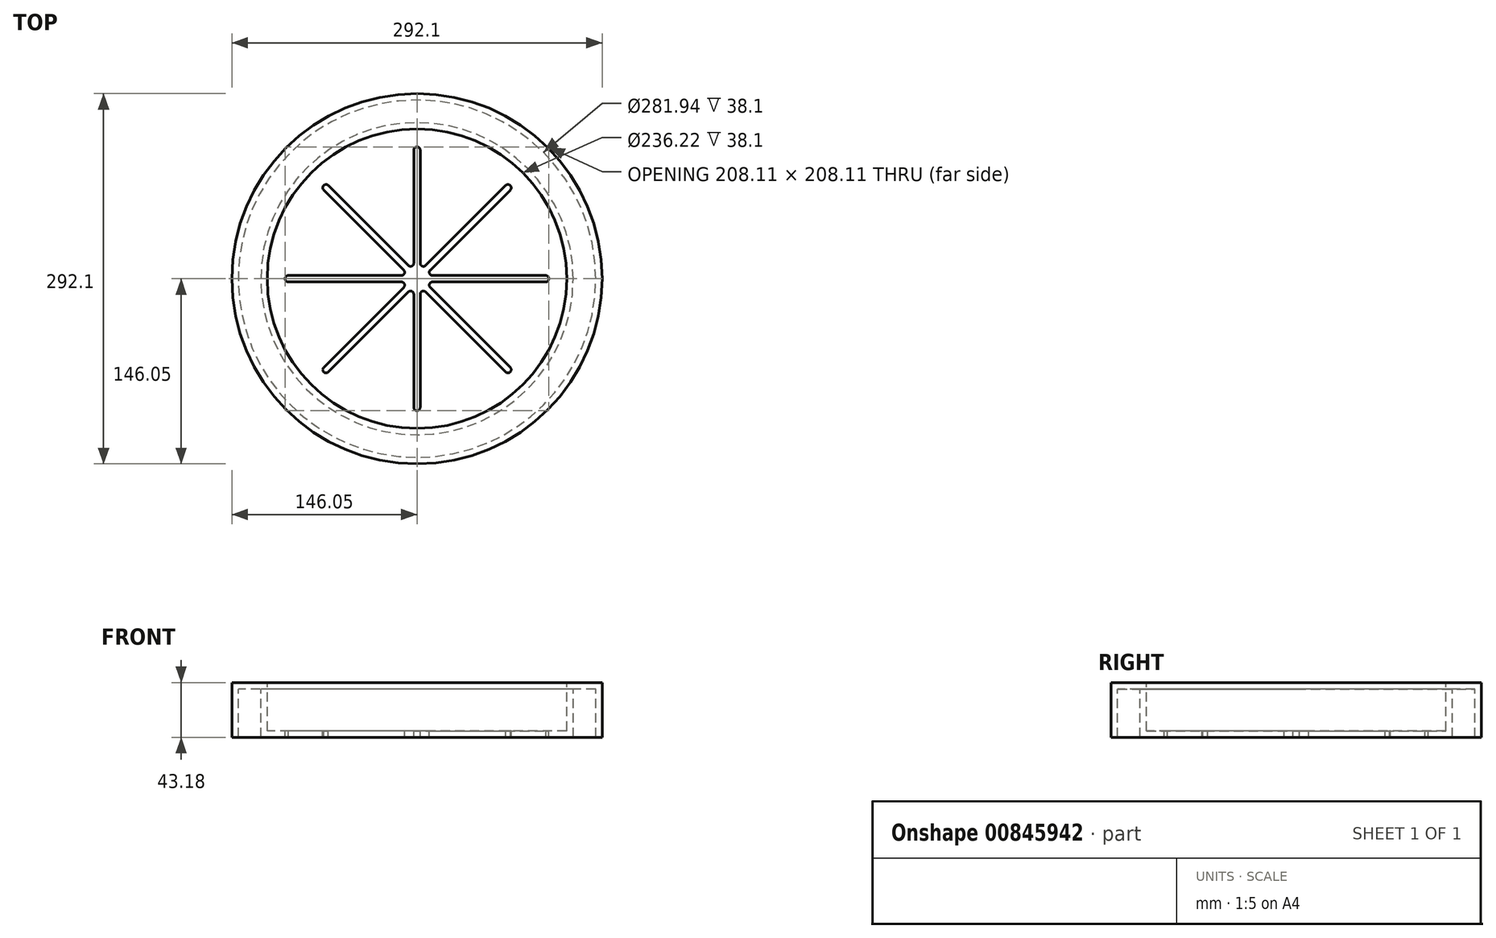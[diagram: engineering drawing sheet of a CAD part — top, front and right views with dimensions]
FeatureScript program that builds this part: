
annotation { "Feature Type Name" : "Feature", "Feature Type Description" : "" }
export const myFeature = defineFeature(function(context is Context, id is Id, definition is map)
    precondition{}
    {
        {
            var Q0;
            Q0=qCreatedBy(makeId("Front.planeOp"),FACE);
            var sketch = newSketch(context, id + "F0", { "sketchPlane" : qUnion([Q0])});
            skLineSegment(sketch, "E0", {"start": v(0, 0) * mm, "end": v(-123.2, 0) * mm});
            skLineSegment(sketch, "E1", {"start": v(-146.05, 0) * mm, "end": v(-146.05, 43.18) * mm});
            skLineSegment(sketch, "E2", {"start": v(-146.05, 43.18) * mm, "end": v(-118.11, 43.18) * mm});
            skLineSegment(sketch, "E3", {"start": v(-118.11, 43.18) * mm, "end": v(-118.11, 5.08) * mm});
            skLineSegment(sketch, "E4", {"start": v(-118.11, 5.08) * mm, "end": v(0, 5.08) * mm});
            skLineSegment(sketch, "E5", {"start": v(0, 5.08) * mm, "end": v(0, 0) * mm});
            skLineSegment(sketch, "E6", {"start": v(-146.05, 0) * mm, "end": v(-140.97, 0) * mm});
            skLineSegment(sketch, "E7", {"start": v(-140.97, 0) * mm, "end": v(-140.97, 38.1) * mm});
            skLineSegment(sketch, "E8", {"start": v(-140.97, 38.1) * mm, "end": v(-123.2, 38.1) * mm});
            skLineSegment(sketch, "E9", {"start": v(-123.2, 38.1) * mm, "end": v(-123.2, 0) * mm});
            skLineSegment(sketch, "E10.trimOffspring", {"start": v(-140.97, 0) * mm, "end": v(-146.05, 0) * mm});
            skSolve(sketch);
        }
        {
            var Q0;
            Q0=makeQuery(id+"F0.imprint","IMPRINT",FACE,{"disambiguationData":[TD([[makeQuery(id+"F0.imprint","IMPRINT",EDGE,{"derivedFrom":sQuery(id+"F0.wireOp",EDGE,"E0")}),-1.0]])]});
            var Q1;
            Q1=sQuery(id+"F0.wireOp",EDGE,"E5");
            revolve(context, id + "F1", {"surfaceOperationType" : NewSurfaceOperationType.NEW, "entities" : qUnion([Q0]), "axis" : qUnion([Q1]), "revolveType" : RevolveType.FULL});
        }
        {
            var Q0;
            Q0=makeQuery(id+"F1.opRevolve","SWEPT_FACE",FACE,{"disambiguationData":[OSD([sQuery(id+"F0.wireOp",EDGE,"E4")])]});
            var sketch = newSketch(context, id + "F2", { "sketchPlane" : qUnion([Q0])});
            skArc(sketch, "E11", {"start": v(2.54, 101.43) * mm, "mid": v(0, 104.05) * mm, "end": v(-2.54, 101.43) * mm});
            skArc(sketch, "E12.1.0", {"start": v(-69.92, 73.52) * mm, "mid": v(-73.58, 73.58) * mm, "end": v(-73.52, 69.92) * mm});
            skArc(sketch, "E12.2.0", {"start": v(-101.43, 2.54) * mm, "mid": v(-104.05, 0) * mm, "end": v(-101.43, -2.54) * mm});
            skArc(sketch, "E12.3.0", {"start": v(-73.52, -69.92) * mm, "mid": v(-73.58, -73.58) * mm, "end": v(-69.92, -73.52) * mm});
            skArc(sketch, "E12.4.0", {"start": v(-2.54, -101.43) * mm, "mid": v(0, -104.05) * mm, "end": v(2.54, -101.43) * mm});
            skArc(sketch, "E12.5.0", {"start": v(69.92, -73.52) * mm, "mid": v(73.58, -73.58) * mm, "end": v(73.52, -69.92) * mm});
            skArc(sketch, "E12.6.0", {"start": v(101.43, -2.54) * mm, "mid": v(104.05, 0) * mm, "end": v(101.43, 2.54) * mm});
            skArc(sketch, "E12.7.0", {"start": v(73.52, 69.92) * mm, "mid": v(73.58, 73.58) * mm, "end": v(69.92, 73.52) * mm});
            skLineSegment(sketch, "E13.trimOffspring", {"start": v(-6.88, -10.47) * mm, "end": v(-70.05, -73.64) * mm});
            skLineSegment(sketch, "E14.trimOffspring", {"start": v(6.88, -10.47) * mm, "end": v(70.05, -73.64) * mm});
            skLineSegment(sketch, "E15.trimOffspring", {"start": v(2.54, -12.26) * mm, "end": v(2.54, -101.6) * mm});
            skLineSegment(sketch, "E16.trimOffspring", {"start": v(12.26, -2.54) * mm, "end": v(101.6, -2.54) * mm});
            skLineSegment(sketch, "E17.trimOffspring", {"start": v(10.47, -6.88) * mm, "end": v(73.64, -70.05) * mm});
            skLineSegment(sketch, "E18.trimOffspring", {"start": v(12.26, 2.54) * mm, "end": v(101.6, 2.54) * mm});
            skLineSegment(sketch, "E19.trimOffspring", {"start": v(2.54, 12.26) * mm, "end": v(2.54, 101.6) * mm});
            skLineSegment(sketch, "E20.trimOffspring", {"start": v(10.47, 6.88) * mm, "end": v(73.64, 70.05) * mm});
            skLineSegment(sketch, "E21.trimOffspring", {"start": v(6.88, 10.47) * mm, "end": v(70.05, 73.64) * mm});
            skLineSegment(sketch, "E22.trimOffspring", {"start": v(-6.88, 10.47) * mm, "end": v(-70.05, 73.64) * mm});
            skLineSegment(sketch, "E23.trimOffspring", {"start": v(-2.54, 12.26) * mm, "end": v(-2.54, 101.6) * mm});
            skLineSegment(sketch, "E24.trimOffspring", {"start": v(-12.26, 2.54) * mm, "end": v(-101.6, 2.54) * mm});
            skLineSegment(sketch, "E25.trimOffspring", {"start": v(-10.47, 6.88) * mm, "end": v(-73.64, 70.05) * mm});
            skLineSegment(sketch, "E26.trimOffspring", {"start": v(-12.26, -2.54) * mm, "end": v(-101.6, -2.54) * mm});
            skLineSegment(sketch, "E27.trimOffspring", {"start": v(-10.47, -6.88) * mm, "end": v(-73.64, -70.05) * mm});
            skLineSegment(sketch, "E28.trimOffspring", {"start": v(-2.54, -12.26) * mm, "end": v(-2.54, -101.6) * mm});
            skArc(sketch, "E29", {"start": v(2.54, 12.26) * mm, "mid": v(4.1, 9.92) * mm, "end": v(6.88, 10.47) * mm});
            skArc(sketch, "E30.1.0", {"start": v(-6.88, 10.47) * mm, "mid": v(-4.1, 9.92) * mm, "end": v(-2.54, 12.26) * mm});
            skArc(sketch, "E30.2.0", {"start": v(-12.26, 2.54) * mm, "mid": v(-9.92, 4.1) * mm, "end": v(-10.47, 6.88) * mm});
            skArc(sketch, "E30.3.0", {"start": v(-10.47, -6.88) * mm, "mid": v(-9.92, -4.1) * mm, "end": v(-12.26, -2.54) * mm});
            skArc(sketch, "E30.4.0", {"start": v(-2.54, -12.26) * mm, "mid": v(-4.1, -9.92) * mm, "end": v(-6.88, -10.47) * mm});
            skArc(sketch, "E30.5.0", {"start": v(6.88, -10.47) * mm, "mid": v(4.1, -9.92) * mm, "end": v(2.54, -12.26) * mm});
            skArc(sketch, "E30.6.0", {"start": v(12.26, -2.54) * mm, "mid": v(9.92, -4.1) * mm, "end": v(10.47, -6.88) * mm});
            skArc(sketch, "E30.7.0", {"start": v(10.47, 6.88) * mm, "mid": v(9.92, 4.1) * mm, "end": v(12.26, 2.54) * mm});
            skPoint(sketch, "E30.center", {"position": v(0, 0) * mm});
            skSolve(sketch);
        }
        {
            var Q0;
            {var subQ3=sQuery(id+"F2.wireOp",EDGE,"E29");Q0=makeQuery(id+"F2.imprint","IMPRINT",FACE,{"disambiguationData":[TD([[makeQuery(id+"F2.imprint","IMPRINT",EDGE,{"derivedFrom":subQ3}),-1.0]])]});}
            extrude(context, id + "F3", {"entities" : qUnion([Q0]), "operationType" : NewBodyOperationType.REMOVE, "oppositeDirection" : true, "depth" : 25.4 * mm, "offsetDistance" : 25.4 * mm});
        }
    });
